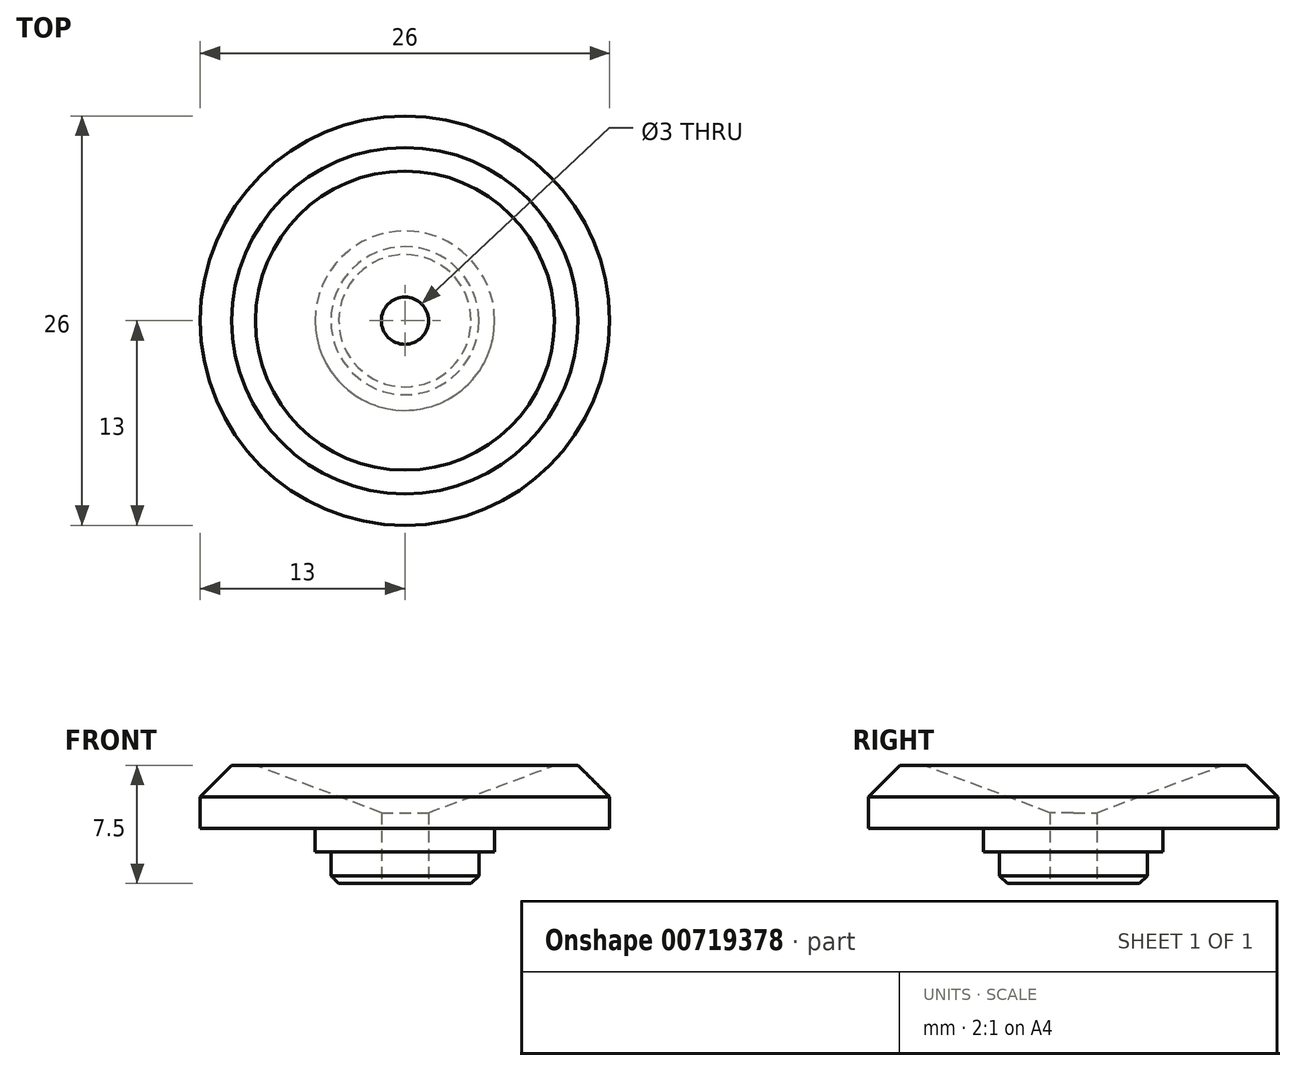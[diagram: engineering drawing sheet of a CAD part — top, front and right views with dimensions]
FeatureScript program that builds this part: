
annotation { "Feature Type Name" : "Feature", "Feature Type Description" : "" }
export const myFeature = defineFeature(function(context is Context, id is Id, definition is map)
    precondition{}
    {
        {
            var Q0;
            Q0=qCreatedBy(makeId("Top.planeOp"),FACE);
            var sketch = newSketch(context, id + "F0", { "sketchPlane" : qUnion([Q0])});
            skCircle(sketch, "E0", {"center": v(0, 0) * mm, "radius": 13 * mm});
            skLineSegment(sketch, "E1", {"start": v(0, 33.5) * mm, "end": v(0, -39.1) * mm, "construction": true});
            skLineSegment(sketch, "E2", {"start": v(30.36, 0) * mm, "end": v(-36.49, 0) * mm, "construction": true});
            skSolve(sketch);
        }
        {
            var Q0;
            Q0=qSketchRegion(id+"F0",true);
            extrude(context, id + "F1", {"entities" : qUnion([Q0]), "depth" : 4 * mm, "offsetDistance" : 25 * mm});
        }
        {
            var Q0;
            Q0=makeQuery(id+"F1.opExtrude","CAP_EDGE",EDGE,{"disambiguationData":[OSD([sQuery(id+"F0.wireOp",EDGE,"E0")])],"isStart":false});
            chamfer(context, id + "F2", {"entities" : qUnion([Q0]), "width" : 2 * mm, "tangentPropagation" : true});
        }
        {
            var Q0;
            Q0=makeQuery(id+"F1.opExtrude","CAP_FACE",FACE,{"disambiguationData":[OSD([sQuery(id+"F0.wireOp",EDGE,"E0")])],"isStart":true});
            var sketch = newSketch(context, id + "F3", { "sketchPlane" : qUnion([Q0])});
            skCircle(sketch, "E3", {"center": v(0, 0) * mm, "radius": 4.7 * mm});
            skSolve(sketch);
        }
        {
            var Q0;
            Q0=qSketchRegion(id+"F3",true);
            extrude(context, id + "F4", {"entities" : qUnion([Q0]), "operationType" : NewBodyOperationType.ADD, "depth" : 3.5 * mm, "offsetDistance" : 25 * mm});
        }
        {
            var Q0;
            Q0=makeQuery(id+"F4.opExtrude","CAP_EDGE",EDGE,{"disambiguationData":[OSD([sQuery(id+"F3.wireOp",EDGE,"E3")])],"isStart":false});
            chamfer(context, id + "F5", {"entities" : qUnion([Q0]), "width" : .5 * mm, "tangentPropagation" : true});
        }
        {
            var Q0;
            Q0=makeQuery(id+"F4.opExtrude","CAP_FACE",FACE,{"disambiguationData":[OSD([sQuery(id+"F3.wireOp",EDGE,"E3")])],"isStart":false});
            var sketch = newSketch(context, id + "F6", { "sketchPlane" : qUnion([Q0])});
            skCircle(sketch, "E4", {"center": v(0, 0) * mm, "radius": 1.5 * mm});
            skSolve(sketch);
        }
        {
            var Q0;
            Q0=qSketchRegion(id+"F6",true);
            extrude(context, id + "F7", {"entities" : qUnion([Q0]), "operationType" : NewBodyOperationType.REMOVE, "oppositeDirection" : true, "depth" : 25 * mm, "offsetDistance" : 25 * mm});
        }
        {
            var Q0;
            Q0=makeQuery(id+"F1.opExtrude","CAP_FACE",FACE,{"disambiguationData":[OSD([sQuery(id+"F0.wireOp",EDGE,"E0")])],"isStart":true});
            var sketch = newSketch(context, id + "F8", { "sketchPlane" : qUnion([Q0])});
            skCircle(sketch, "E5.0", {"center": v(0, 0) * mm, "radius": 5.7 * mm});
            skCircle(sketch, "E6.0", {"center": v(0, 0) * mm, "radius": 4.7 * mm});
            skSolve(sketch);
        }
        {
            var Q0;
            Q0=qSketchRegion(id+"F8",true);
            extrude(context, id + "F9", {"entities" : qUnion([Q0]), "operationType" : NewBodyOperationType.ADD, "depth" : 1.5 * mm, "offsetDistance" : 25 * mm});
        }
        {
            var Q0;
            Q0=makeQuery(id+"F7.boolean.opBoolean","INTERSECT",EDGE,{"derivedFrom":[makeQuery(id+"F1.opExtrude","CAP_FACE",FACE,{"disambiguationData":[OSD([sQuery(id+"F0.wireOp",EDGE,"E0")])],"isStart":false}),makeQuery(id+"F7.opExtrude","SWEPT_FACE",FACE,{"disambiguationData":[OSD([sQuery(id+"F6.wireOp",EDGE,"E4")])]})]});
            chamfer(context, id + "F10", {"entities" : qUnion([Q0]), "chamferType" : ChamferType.TWO_OFFSETS, "width1" : 3 * mm, "oppositeDirection" : false, "width2" : 8 * mm, "tangentPropagation" : true});
        }
    });
